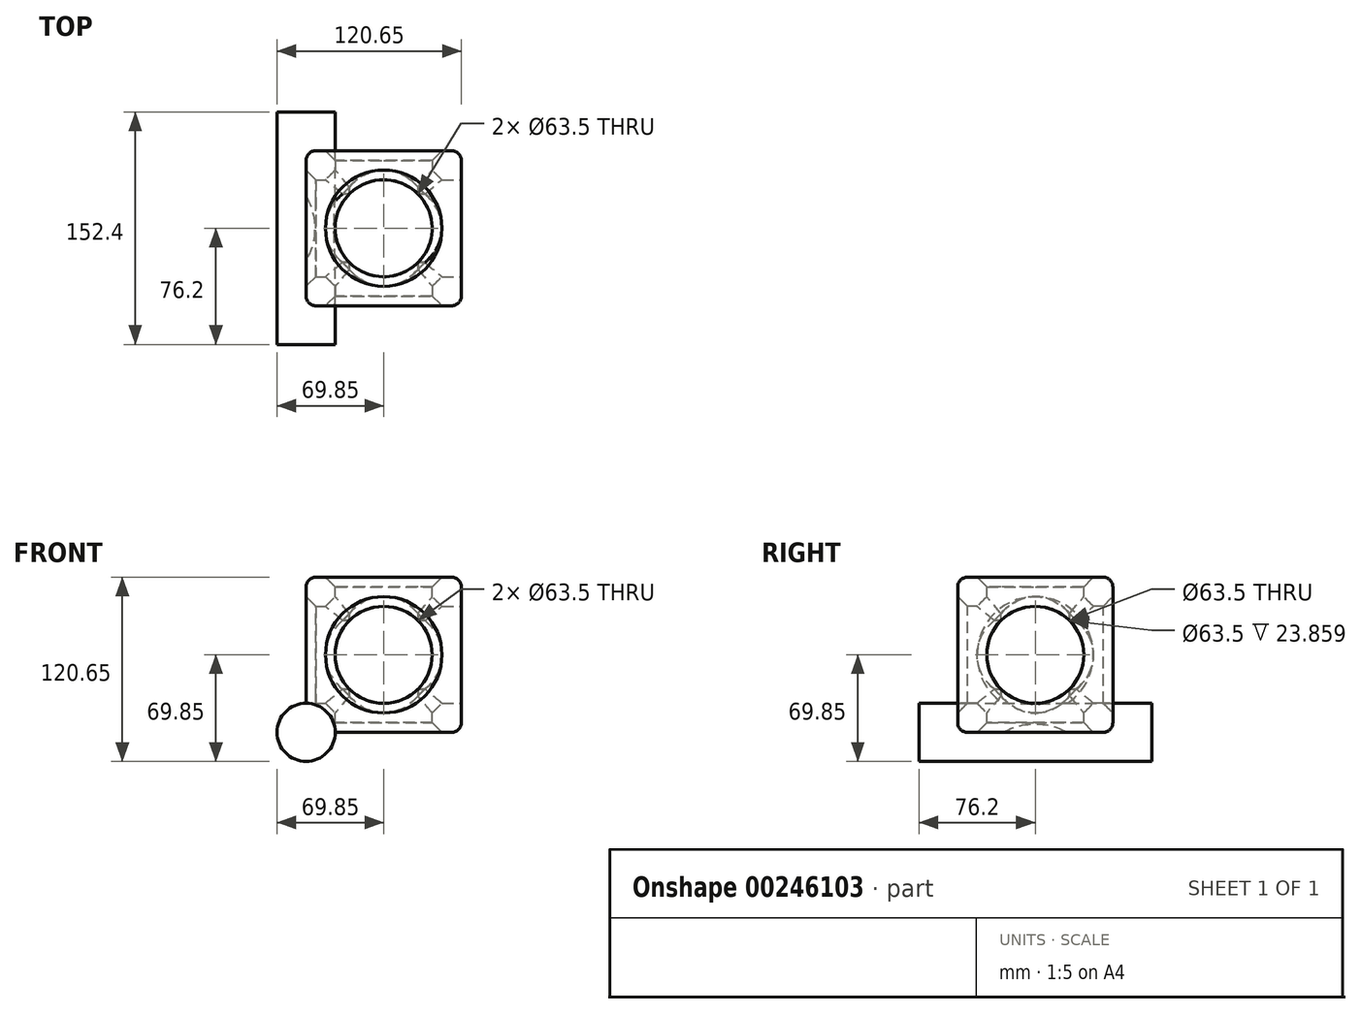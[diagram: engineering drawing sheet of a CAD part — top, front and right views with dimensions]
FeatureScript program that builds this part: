
annotation { "Feature Type Name" : "Feature", "Feature Type Description" : "" }
export const myFeature = defineFeature(function(context is Context, id is Id, definition is map)
    precondition{}
    {
        {
            var Q0;
            Q0=qCreatedBy(makeId("Front.planeOp"),FACE);
            var sketch = newSketch(context, id + "F0", { "sketchPlane" : qUnion([Q0])});
            skLineSegment(sketch, "E0", {"start": v(0, 0) * mm, "end": v(101.6, 0) * mm});
            skLineSegment(sketch, "E1", {"start": v(101.6, 0) * mm, "end": v(101.6, 101.6) * mm});
            skLineSegment(sketch, "E2", {"start": v(101.6, 101.6) * mm, "end": v(0, 101.6) * mm});
            skLineSegment(sketch, "E3", {"start": v(0, 101.6) * mm, "end": v(0, 0) * mm});
            skSolve(sketch);
        }
        {
            var Q0;
            Q0=makeQuery(id+"F0.imprint","IMPRINT",FACE,{"disambiguationData":[TD([[makeQuery(id+"F0.imprint","IMPRINT",EDGE,{"derivedFrom":sQuery(id+"F0.wireOp",EDGE,"E0")}),1.0]])]});
            extrude(context, id + "F1", {"entities" : qUnion([Q0]), "depth" : 101.6 * mm});
        }
        {
            var Q0;
            Q0=makeQuery(id+"F1.opExtrude","CAP_FACE",FACE,{"disambiguationData":[OSD([sQuery(id+"F0.wireOp",EDGE,"E0"),sQuery(id+"F0.wireOp",EDGE,"E1"),sQuery(id+"F0.wireOp",EDGE,"E2"),sQuery(id+"F0.wireOp",EDGE,"E3")])],"isStart":false});
            var sketch = newSketch(context, id + "F2", { "sketchPlane" : qUnion([Q0])});
            skCircle(sketch, "E4", {"center": v(50.8, 50.8) * mm, "radius": 31.75 * mm});
            skPoint(sketch, "E5.orphan", {"position": v(50.8, 101.6) * mm});
            skPoint(sketch, "E6.end.orphan", {"position": v(50.8, 0) * mm});
            skSolve(sketch);
        }
        {
            var Q0;
            Q0=makeQuery(id+"F2.imprint","IMPRINT",FACE,{"disambiguationData":[TD([[makeQuery(id+"F2.imprint","IMPRINT",EDGE,{"derivedFrom":sQuery(id+"F2.wireOp",EDGE,"E4")}),1.0]])]});
            extrude(context, id + "F3", {"entities" : qUnion([Q0]), "operationType" : NewBodyOperationType.REMOVE, "oppositeDirection" : true, "depth" : 101.6 * mm});
        }
        {
            var Q0;
            Q0=makeQuery(id+"F1.opExtrude","SWEPT_FACE",FACE,{"disambiguationData":[OSD([sQuery(id+"F0.wireOp",EDGE,"E2")])]});
            var sketch = newSketch(context, id + "F4", { "sketchPlane" : qUnion([Q0])});
            skCircle(sketch, "E7", {"center": v(50.8, -50.8) * mm, "radius": 31.75 * mm});
            skPoint(sketch, "E8.orphan", {"position": v(50.8, 0) * mm});
            skPoint(sketch, "E9.end.orphan", {"position": v(50.8, -101.6) * mm});
            skSolve(sketch);
        }
        {
            var Q0;
            Q0=makeQuery(id+"F4.imprint","IMPRINT",FACE,{"disambiguationData":[TD([[makeQuery(id+"F4.imprint","IMPRINT",EDGE,{"derivedFrom":sQuery(id+"F4.wireOp",EDGE,"E7")}),1.0]])]});
            extrude(context, id + "F5", {"entities" : qUnion([Q0]), "operationType" : NewBodyOperationType.REMOVE, "oppositeDirection" : true, "depth" : 101.6 * mm});
        }
        {
            var Q0;
            Q0=makeQuery(id+"F1.opExtrude","SWEPT_FACE",FACE,{"disambiguationData":[OSD([sQuery(id+"F0.wireOp",EDGE,"E1")])]});
            var sketch = newSketch(context, id + "F6", { "sketchPlane" : qUnion([Q0])});
            skCircle(sketch, "E10", {"center": v(-50.8, 50.8) * mm, "radius": 31.75 * mm});
            skPoint(sketch, "E11.orphan", {"position": v(-50.8, 101.6) * mm});
            skPoint(sketch, "E12.end.orphan", {"position": v(-50.8, 0) * mm});
            skSolve(sketch);
        }
        {
            var Q0;
            Q0=makeQuery(id+"F6.imprint","IMPRINT",FACE,{"disambiguationData":[TD([[makeQuery(id+"F6.imprint","IMPRINT",EDGE,{"derivedFrom":sQuery(id+"F6.wireOp",EDGE,"E10")}),1.0]])]});
            extrude(context, id + "F7", {"entities" : qUnion([Q0]), "operationType" : NewBodyOperationType.REMOVE, "oppositeDirection" : true, "depth" : 101.6 * mm});
        }
        {
            var Q0;
            Q0=makeQuery(id+"F1.opExtrude","CAP_EDGE",EDGE,{"disambiguationData":[OSD([sQuery(id+"F0.wireOp",EDGE,"E2")])],"isStart":false});
            var Q1;
            Q1=makeQuery(id+"F1.opExtrude","SWEPT_EDGE",EDGE,{"disambiguationData":[OSD([sQuery(id+"F0.wireOp",EDGE,"E2"),sQuery(id+"F0.wireOp",EDGE,"E3")])]});
            var Q2;
            Q2=makeQuery(id+"F1.opExtrude","CAP_EDGE",EDGE,{"disambiguationData":[OSD([sQuery(id+"F0.wireOp",EDGE,"E3")])],"isStart":false});
            var Q3;
            Q3=makeQuery(id+"F1.opExtrude","SWEPT_EDGE",EDGE,{"disambiguationData":[OSD([sQuery(id+"F0.wireOp",EDGE,"E0"),sQuery(id+"F0.wireOp",EDGE,"E3")])]});
            var Q4;
            Q4=makeQuery(id+"F1.opExtrude","CAP_EDGE",EDGE,{"disambiguationData":[OSD([sQuery(id+"F0.wireOp",EDGE,"E0")])],"isStart":false});
            var Q5;
            Q5=makeQuery(id+"F1.opExtrude","CAP_EDGE",EDGE,{"disambiguationData":[OSD([sQuery(id+"F0.wireOp",EDGE,"E3")])],"isStart":true});
            var Q6;
            Q6=makeQuery(id+"F1.opExtrude","CAP_EDGE",EDGE,{"disambiguationData":[OSD([sQuery(id+"F0.wireOp",EDGE,"E1")])],"isStart":false});
            var Q7;
            Q7=makeQuery(id+"F1.opExtrude","SWEPT_EDGE",EDGE,{"disambiguationData":[OSD([sQuery(id+"F0.wireOp",EDGE,"E0"),sQuery(id+"F0.wireOp",EDGE,"E1")])]});
            var Q8;
            Q8=makeQuery(id+"F1.opExtrude","SWEPT_EDGE",EDGE,{"disambiguationData":[OSD([sQuery(id+"F0.wireOp",EDGE,"E1"),sQuery(id+"F0.wireOp",EDGE,"E2")])]});
            var Q9;
            Q9=makeQuery(id+"F1.opExtrude","CAP_EDGE",EDGE,{"disambiguationData":[OSD([sQuery(id+"F0.wireOp",EDGE,"E1")])],"isStart":true});
            var Q10;
            Q10=makeQuery(id+"F1.opExtrude","CAP_EDGE",EDGE,{"disambiguationData":[OSD([sQuery(id+"F0.wireOp",EDGE,"E2")])],"isStart":true});
            var Q11;
            Q11=makeQuery(id+"F1.opExtrude","CAP_EDGE",EDGE,{"disambiguationData":[OSD([sQuery(id+"F0.wireOp",EDGE,"E0")])],"isStart":true});
            fillet(context, id + "F8", {"entities" : qUnion([Q0, Q1, Q2, Q3, Q4, Q5, Q6, Q7, Q8, Q9, Q10, Q11]), "radius" : 6.35 * mm, "tangentPropagation" : true, "allowEdgeOverflow" : false});
        }
        {
            var Q0;
            {var subQ0=makeQuery(id+"F5.opExtrude","SWEPT_FACE",FACE,{"disambiguationData":[OSD([sQuery(id+"F4.wireOp",EDGE,"E7")])]});Q0=makeQuery(id+"F5.boolean.opBoolean","COPY",FACE,{"disambiguationData":[TD([makeQuery(id+"F1.opExtrude","SWEPT_FACE",FACE,{"disambiguationData":[OSD([sQuery(id+"F0.wireOp",EDGE,"E2")])]})])],"derivedFrom":subQ0});}
            var Q1;
            {var subQ0=makeQuery(id+"F3.boolean.opBoolean","COPY",FACE,{"derivedFrom":makeQuery(id+"F3.opExtrude","SWEPT_FACE",FACE,{"disambiguationData":[OSD([sQuery(id+"F2.wireOp",EDGE,"E4")])]})});Q1=makeQuery(id+"F5.boolean.opBoolean","SPLIT",FACE,{"disambiguationData":[TD([makeQuery(id+"F1.opExtrude","CAP_FACE",FACE,{"disambiguationData":[OSD([sQuery(id+"F0.wireOp",EDGE,"E0"),sQuery(id+"F0.wireOp",EDGE,"E1"),sQuery(id+"F0.wireOp",EDGE,"E2"),sQuery(id+"F0.wireOp",EDGE,"E3")])],"isStart":true})])],"derivedFrom":subQ0});}
            var Q2;
            Q2=makeQuery(id+"F5.boolean.opBoolean","COPY",EDGE,{"derivedFrom":makeQuery(id+"F5.opExtrude","CAP_EDGE",EDGE,{"disambiguationData":[OSD([sQuery(id+"F4.wireOp",EDGE,"E7")])],"isStart":false})});
            var Q3;
            {var subQ0=makeQuery(id+"F5.opExtrude","SWEPT_FACE",FACE,{"disambiguationData":[OSD([sQuery(id+"F4.wireOp",EDGE,"E7")])]});Q3=makeQuery(id+"F5.boolean.opBoolean","COPY",FACE,{"disambiguationData":[TD([makeQuery(id+"F1.opExtrude","SWEPT_FACE",FACE,{"disambiguationData":[OSD([sQuery(id+"F0.wireOp",EDGE,"E0")])]})])],"derivedFrom":subQ0});}
            var Q4;
            Q4=makeQuery(id+"F7.boolean.opBoolean","COPY",FACE,{"disambiguationData":[TD([makeQuery(id+"F1.opExtrude","SWEPT_FACE",FACE,{"disambiguationData":[OSD([sQuery(id+"F0.wireOp",EDGE,"E3")])]})])],"derivedFrom":makeQuery(id+"F7.opExtrude","SWEPT_FACE",FACE,{"disambiguationData":[OSD([sQuery(id+"F6.wireOp",EDGE,"E10")])]})});
            var Q5;
            Q5=makeQuery(id+"F7.boolean.opBoolean","COPY",EDGE,{"derivedFrom":makeQuery(id+"F7.opExtrude","CAP_EDGE",EDGE,{"disambiguationData":[OSD([sQuery(id+"F6.wireOp",EDGE,"E10")])],"isStart":true})});
            var Q6;
            {var subQ0=makeQuery(id+"F3.boolean.opBoolean","COPY",FACE,{"derivedFrom":makeQuery(id+"F3.opExtrude","SWEPT_FACE",FACE,{"disambiguationData":[OSD([sQuery(id+"F2.wireOp",EDGE,"E4")])]})});Q6=makeQuery(id+"F5.boolean.opBoolean","SPLIT",FACE,{"disambiguationData":[TD([makeQuery(id+"F1.opExtrude","CAP_FACE",FACE,{"disambiguationData":[OSD([sQuery(id+"F0.wireOp",EDGE,"E0"),sQuery(id+"F0.wireOp",EDGE,"E1"),sQuery(id+"F0.wireOp",EDGE,"E2"),sQuery(id+"F0.wireOp",EDGE,"E3")])],"isStart":false})])],"derivedFrom":subQ0});}
            chamfer(context, id + "F9", {"entities" : qUnion([Q0, Q1, Q2, Q3, Q4, Q5, Q6]), "width" : 6.35 * mm, "tangentPropagation" : true});
        }
        {
            var Q0;
            Q0=qCreatedBy(makeId("Front.planeOp"),FACE);
            cPlane(context, id + "F10", {"entities" : qUnion([Q0]), "cplaneType" : CPlaneType.OFFSET, "offset" : 101.6 * mm, "width" : 152.4 * mm, "height" : 152.4 * mm});
        }
        {
            var Q0;
            Q0=qCreatedBy(id+"F10.planeOp",FACE);
            var sketch = newSketch(context, id + "F11", { "sketchPlane" : qUnion([Q0])});
            skCircle(sketch, "E13", {"center": v(0, 0) * mm, "radius": 19.05 * mm});
            skSolve(sketch);
        }
        {
            var Q0;
            Q0=makeQuery(id+"F11.imprint","IMPRINT",FACE,{"disambiguationData":[TD([[makeQuery(id+"F11.imprint","IMPRINT",EDGE,{"derivedFrom":sQuery(id+"F11.wireOp",EDGE,"E13")}),1.0]])]});
            extrude(context, id + "F12", {"entities" : qUnion([Q0]), "operationType" : NewBodyOperationType.ADD, "depth" : 25.4 * mm, "hasSecondDirection" : true, "secondDirectionOppositeDirection" : true, "secondDirectionDepth" : 127 * mm});
        }
    });
